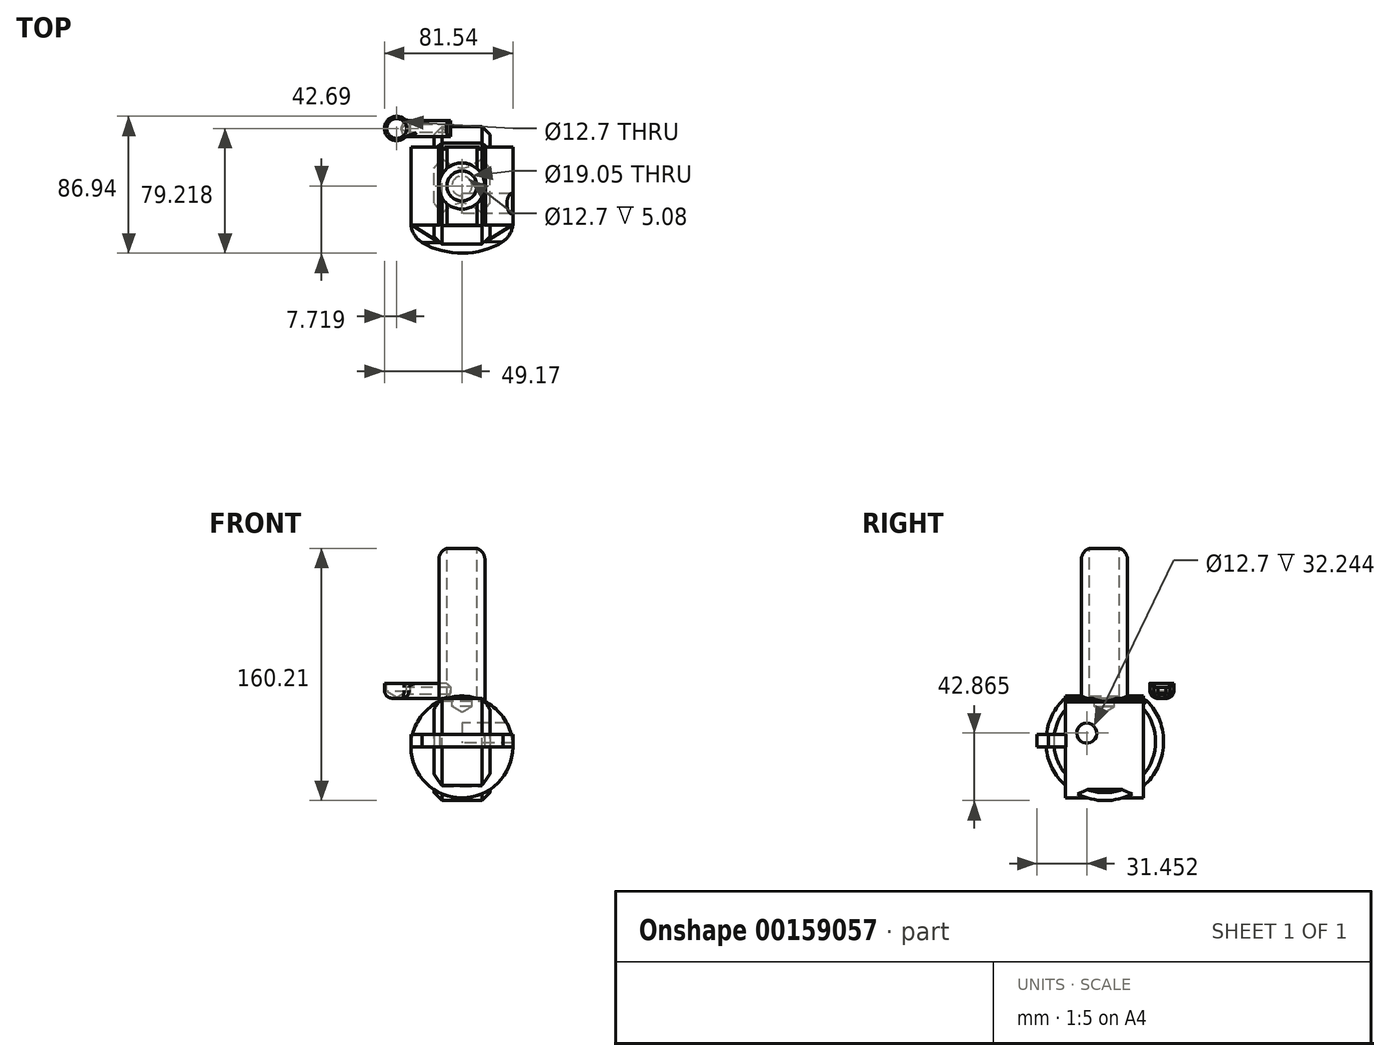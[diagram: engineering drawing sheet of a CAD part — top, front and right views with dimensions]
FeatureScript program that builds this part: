
annotation { "Feature Type Name" : "Feature", "Feature Type Description" : "" }
export const myFeature = defineFeature(function(context is Context, id is Id, definition is map)
    precondition{}
    {
        {
            var Q0;
            Q0=qCreatedBy(makeId("Top.planeOp"),FACE);
            var sketch = newSketch(context, id + "F0", { "sketchPlane" : qUnion([Q0])});
            skCircle(sketch, "E0", {"center": v(0, 0) * mm, "radius": 14.63 * mm});
            skSolve(sketch);
        }
        {
            var Q0;
            Q0=makeQuery(id+"F0.imprint","IMPRINT",FACE,{"disambiguationData":[TD([[makeQuery(id+"F0.imprint","IMPRINT",EDGE,{"derivedFrom":sQuery(id+"F0.wireOp",EDGE,"E0")}),1.0]])]});
            extrude(context, id + "F1", {"entities" : qUnion([Q0]), "depth" : 95.25 * mm});
        }
        {
            var Q0;
            Q0=qCreatedBy(makeId("Right.planeOp"),FACE);
            var sketch = newSketch(context, id + "F2", { "sketchPlane" : qUnion([Q0])});
            skArc(sketch, "E1", {"start": v(-25.08, 0) * mm, "mid": v(0.22, -64.96) * mm, "end": v(25.52, 0) * mm});
            skLineSegment(sketch, "E2", {"start": v(-25.08, 0) * mm, "end": v(25.52, 0) * mm});
            skSolve(sketch);
        }
        {
            var Q0;
            Q0 = qSketchRegion(id + "F2", true);
            extrude(context, id + "F3", {"entities" : qUnion([Q0]), "operationType" : NewBodyOperationType.ADD, "endBound" : BoundingType.SYMMETRIC, "oppositeDirection" : true, "depth" : 35.56 * mm});
        }
        {
            var Q0;
            Q0=makeQuery(id+"F1.opExtrude","CAP_FACE",FACE,{"disambiguationData":[OSD([sQuery(id+"F0.wireOp",EDGE,"E0")])],"isStart":false});
            var sketch = newSketch(context, id + "F4", { "sketchPlane" : qUnion([Q0])});
            skCircle(sketch, "E3", {"center": v(0, 0) * mm, "radius": 10 * mm});
            skSolve(sketch);
        }
        {
            var Q0;
            Q0=sQuery(id+"F4.wireOp",VERTEX,"E3.center");
            var Q1;
            Q1=makeQuery(id+"F1.opExtrude","SWEPT_BODY",BODY,{"disambiguationData":[OSD([sQuery(id+"F0.wireOp",EDGE,"E0")])]});
            hole(context, id + "F5", {"style" : HoleStyle.SIMPLE, "endStyle" : HoleEndStyle.BLIND, "holeDiameter" : 19.05 * mm, "holeDepth" : 139.7 * mm, "locations" : qUnion([Q0]), "scope" : qUnion([Q1])});
        }
        {
            var Q0;
            Q0=makeQuery(id+"F3.opExtrude","CAP_FACE",FACE,{"disambiguationData":[OSD([sQuery(id+"F2.wireOp",EDGE,"E1"),sQuery(id+"F2.wireOp",EDGE,"E2")])],"isStart":true});
            var sketch = newSketch(context, id + "F6", { "sketchPlane" : qUnion([Q0])});
            skCircle(sketch, "E4", {"center": v(18.07, -19.67) * mm, "radius": 8.9 * mm});
            skSolve(sketch);
        }
        {
            var Q0;
            Q0=sQuery(id+"F6.wireOp",VERTEX,"E4.center");
            var Q1;
            Q1=makeQuery(id+"F1.opExtrude","SWEPT_BODY",BODY,{"disambiguationData":[OSD([sQuery(id+"F0.wireOp",EDGE,"E0")])]});
            hole(context, id + "F7", {"style" : HoleStyle.SIMPLE, "endStyle" : HoleEndStyle.BLIND, "holeDiameter" : 12.7 * mm, "holeDepth" : 30.48 * mm, "locations" : qUnion([Q0]), "scope" : qUnion([Q1])});
        }
        {
            var Q0;
            Q0=qCreatedBy(makeId("Top.planeOp"),FACE);
            var sketch = newSketch(context, id + "F8", { "sketchPlane" : qUnion([Q0])});
            skLineSegment(sketch, "E5", {"start": v(-7.05, 41.62) * mm, "end": v(-35.65, 41.62) * mm});
            skLineSegment(sketch, "E6", {"start": v(-7.05, 41.62) * mm, "end": v(-7.05, 31.44) * mm});
            skLineSegment(sketch, "E7", {"start": v(-7.05, 31.44) * mm, "end": v(-35.65, 31.44) * mm});
            skArc(sketch, "E8", {"start": v(-35.65, 41.62) * mm, "mid": v(-49.17, 36.53) * mm, "end": v(-35.65, 31.44) * mm});
            skSolve(sketch);
        }
        {
            var Q0;
            Q0=makeQuery(id+"F8.imprint","IMPRINT",FACE,{"disambiguationData":[TD([[makeQuery(id+"F8.imprint","IMPRINT",EDGE,{"derivedFrom":sQuery(id+"F8.wireOp",EDGE,"E5")}),1.0]])]});
            extrude(context, id + "F9", {"entities" : qUnion([Q0]), "depth" : 9.52 * mm});
        }
        {
            var Q0;
            Q0=makeQuery(id+"F9.opExtrude","CAP_FACE",FACE,{"disambiguationData":[OSD([sQuery(id+"F8.wireOp",EDGE,"E5"),sQuery(id+"F8.wireOp",EDGE,"E6"),sQuery(id+"F8.wireOp",EDGE,"E7"),sQuery(id+"F8.wireOp",EDGE,"E8")])],"isStart":false});
            var sketch = newSketch(context, id + "F10", { "sketchPlane" : qUnion([Q0])});
            skCircle(sketch, "E9", {"center": v(-41.45, 36.53) * mm, "radius": 4.92 * mm});
            skSolve(sketch);
        }
        {
            var Q0;
            Q0=sQuery(id+"F10.wireOp",VERTEX,"E9.center");
            var Q1;
            Q1=makeQuery(id+"F9.opExtrude","SWEPT_BODY",BODY,{"disambiguationData":[OSD([sQuery(id+"F8.wireOp",EDGE,"E5"),sQuery(id+"F8.wireOp",EDGE,"E6"),sQuery(id+"F8.wireOp",EDGE,"E7"),sQuery(id+"F8.wireOp",EDGE,"E8")])]});
            hole(context, id + "F11", {"style" : HoleStyle.SIMPLE, "endStyle" : HoleEndStyle.BLIND, "holeDiameter" : 12.7 * mm, "holeDepth" : 5.08 * mm, "locations" : qUnion([Q0]), "scope" : qUnion([Q1])});
        }
        {
            var Q0;
            Q0=makeQuery(id+"F9.opExtrude","SWEPT_FACE",FACE,{"disambiguationData":[OSD([sQuery(id+"F8.wireOp",EDGE,"E6")])]});
            var Q1;
            Q1=makeQuery(id+"F11.hole-0.boolean.opBoolean","COPY",FACE,{"derivedFrom":makeQuery(id+"F11.hole-0.opRevolve","SWEPT_FACE",FACE,{"disambiguationData":[OSD([sQuery(id+"F11.hole-0.sketch.wireOp",EDGE,"core_line_2")])]})});
            shell(context, id + "F12", {"entities" : qUnion([Q0, Q1]), "thickness" : 2.54 * mm});
        }
        {
            var Q0;
            Q0=makeQuery(id+"F1.opExtrude","CAP_EDGE",EDGE,{"disambiguationData":[OSD([sQuery(id+"F0.wireOp",EDGE,"E0")])],"isStart":false});
            fillet(context, id + "F13", {"entities" : qUnion([Q0]), "radius" : 7.62 * mm, "tangentPropagation" : true, "allowEdgeOverflow" : false});
        }
        {
            var Q0;
            Q0=makeQuery(id+"F9.opExtrude","CAP_FACE",FACE,{"disambiguationData":[OSD([sQuery(id+"F8.wireOp",EDGE,"E5"),sQuery(id+"F8.wireOp",EDGE,"E6"),sQuery(id+"F8.wireOp",EDGE,"E7"),sQuery(id+"F8.wireOp",EDGE,"E8")])],"isStart":true});
            fillet(context, id + "F14", {"entities" : qUnion([Q0]), "radius" : 5.08 * mm, "tangentPropagation" : true, "allowEdgeOverflow" : false});
        }
        {
            var Q0;
            Q0=makeQuery(id+"F9.opExtrude","CAP_EDGE",EDGE,{"disambiguationData":[OSD([sQuery(id+"F8.wireOp",EDGE,"E6")])],"isStart":false});
            chamfer(context, id + "F15", {"entities" : qUnion([Q0]), "width" : 2.54 * mm, "tangentPropagation" : true});
        }
        {
            var Q0;
            Q0=makeQuery(id+"F9.opExtrude","CAP_EDGE",EDGE,{"disambiguationData":[OSD([sQuery(id+"F8.wireOp",EDGE,"E7")])],"isStart":false});
            var Q1;
            Q1=makeQuery(id+"F9.opExtrude","CAP_EDGE",EDGE,{"disambiguationData":[OSD([sQuery(id+"F8.wireOp",EDGE,"E5")])],"isStart":false});
            fillet(context, id + "F16", {"entities" : qUnion([Q0, Q1]), "radius" : 2.45 * mm, "tangentPropagation" : true, "allowEdgeOverflow" : false});
        }
        {
            var Q0;
            Q0=makeQuery(id+"F14.opFillet","BLEND_EDGE",EDGE,{"blendedFrom":[makeQuery(id+"F9.opExtrude","CAP_EDGE",EDGE,{"disambiguationData":[OSD([sQuery(id+"F8.wireOp",EDGE,"E5")])],"isStart":true}),makeQuery(id+"F9.opExtrude","CAP_EDGE",EDGE,{"disambiguationData":[OSD([sQuery(id+"F8.wireOp",EDGE,"E8")])],"isStart":true})],"blendedInto":[]});
            var Q1;
            Q1=makeQuery(id+"F16.opFillet","BLEND_EDGE",EDGE,{"blendedFrom":[makeQuery(id+"F9.opExtrude","CAP_EDGE",EDGE,{"disambiguationData":[OSD([sQuery(id+"F8.wireOp",EDGE,"E7")])],"isStart":false}),makeQuery(id+"F9.opExtrude","SWEPT_FACE",FACE,{"disambiguationData":[OSD([sQuery(id+"F8.wireOp",EDGE,"E8")])]})],"blendedInto":[makeQuery(id+"F9.opExtrude","SWEPT_FACE",FACE,{"disambiguationData":[OSD([sQuery(id+"F8.wireOp",EDGE,"E8")])]})]});
            var Q2;
            Q2=makeQuery(id+"F9.opExtrude","SWEPT_EDGE",EDGE,{"disambiguationData":[OSD([sQuery(id+"F8.wireOp",EDGE,"E7"),sQuery(id+"F8.wireOp",EDGE,"E8")])]});
            var Q3;
            Q3=makeQuery(id+"F14.opFillet","BLEND_EDGE",EDGE,{"blendedFrom":[makeQuery(id+"F9.opExtrude","CAP_EDGE",EDGE,{"disambiguationData":[OSD([sQuery(id+"F8.wireOp",EDGE,"E7")])],"isStart":true}),makeQuery(id+"F9.opExtrude","CAP_EDGE",EDGE,{"disambiguationData":[OSD([sQuery(id+"F8.wireOp",EDGE,"E8")])],"isStart":true})],"blendedInto":[]});
            var Q4;
            Q4=makeQuery(id+"F16.opFillet","BLEND_EDGE",EDGE,{"blendedFrom":[makeQuery(id+"F9.opExtrude","CAP_EDGE",EDGE,{"disambiguationData":[OSD([sQuery(id+"F8.wireOp",EDGE,"E5")])],"isStart":false}),makeQuery(id+"F9.opExtrude","SWEPT_FACE",FACE,{"disambiguationData":[OSD([sQuery(id+"F8.wireOp",EDGE,"E8")])]})],"blendedInto":[makeQuery(id+"F9.opExtrude","SWEPT_FACE",FACE,{"disambiguationData":[OSD([sQuery(id+"F8.wireOp",EDGE,"E8")])]})]});
            var Q5;
            Q5=makeQuery(id+"F9.opExtrude","SWEPT_EDGE",EDGE,{"disambiguationData":[OSD([sQuery(id+"F8.wireOp",EDGE,"E5"),sQuery(id+"F8.wireOp",EDGE,"E8")])]});
            fillet(context, id + "F17", {"entities" : qUnion([Q0, Q1, Q2, Q3, Q4, Q5]), "radius" : 5.08 * mm, "tangentPropagation" : true, "allowEdgeOverflow" : false});
        }
        {
            var Q0;
            Q0=makeQuery(id+"F3.opExtrude","CAP_EDGE",EDGE,{"disambiguationData":[OSD([sQuery(id+"F2.wireOp",EDGE,"E1")])],"isStart":true});
            var Q1;
            Q1=makeQuery(id+"F3.opExtrude","CAP_EDGE",EDGE,{"disambiguationData":[OSD([sQuery(id+"F2.wireOp",EDGE,"E2")])],"isStart":true});
            var Q2;
            {var subQ0=sQuery(id+"F2.wireOp",EDGE,"E2");var subQ1=sQuery(id+"F2.wireOp",EDGE,"E1");Q2=makeQuery(id+"F3.opExtrude","SWEPT_EDGE",EDGE,{"disambiguationData":[OSD([subQ1,subQ0]),TDD([makeQuery(id+"F2.imprint","INTERSECT",VERTEX,{"disambiguationData":[OD(1.0)],"derivedFrom":[subQ1,subQ0]})])]});}
            var Q3;
            Q3=makeQuery(id+"F3.opExtrude","CAP_EDGE",EDGE,{"disambiguationData":[OSD([sQuery(id+"F2.wireOp",EDGE,"E2")])],"isStart":false});
            var Q4;
            Q4=makeQuery(id+"F3.opExtrude","CAP_EDGE",EDGE,{"disambiguationData":[OSD([sQuery(id+"F2.wireOp",EDGE,"E1")])],"isStart":false});
            chamfer(context, id + "F18", {"entities" : qUnion([Q0, Q1, Q2, Q3, Q4]), "width" : 5.08 * mm, "tangentPropagation" : true});
        }
        {
            var Q0;
            Q0=qCreatedBy(makeId("Front.planeOp"),FACE);
            var sketch = newSketch(context, id + "F19", { "sketchPlane" : qUnion([Q0])});
            skCircle(sketch, "E10", {"center": v(0, -30.9) * mm, "radius": 32.34 * mm});
            skSolve(sketch);
        }
        {
            var Q0;
            Q0 = qSketchRegion(id + "F19", true);
            extrude(context, id + "F20", {"entities" : qUnion([Q0]), "operationType" : NewBodyOperationType.ADD, "endBound" : BoundingType.SYMMETRIC, "depth" : 49.53 * mm});
        }
        {
            var Q0;
            Q0=qCreatedBy(makeId("Right.planeOp"),FACE);
            var sketch = newSketch(context, id + "F21", { "sketchPlane" : qUnion([Q0])});
            skCircle(sketch, "E11", {"center": v(-11.24, -22.1) * mm, "radius": 6.4 * mm});
            skSolve(sketch);
        }
        {
            var Q0;
            Q0=sQuery(id+"F21.wireOp",VERTEX,"E11.center");
            var Q1;
            Q1=makeQuery(id+"F1.opExtrude","SWEPT_BODY",BODY,{"disambiguationData":[OSD([sQuery(id+"F0.wireOp",EDGE,"E0")])]});
            hole(context, id + "F22", {"style" : HoleStyle.SIMPLE, "endStyle" : HoleEndStyle.THROUGH, "oppositeDirection" : true, "holeDiameter" : 12.7 * mm, "locations" : qUnion([Q0]), "scope" : qUnion([Q1]), "isTappedThrough" : true});
        }
        {
            var Q0;
            Q0=qCreatedBy(makeId("Top.planeOp"),FACE);
            var sketch = newSketch(context, id + "F23", { "sketchPlane" : qUnion([Q0])});
            skCircle(sketch, "E12", {"center": v(0, 0) * mm, "radius": 7.96 * mm});
            skSolve(sketch);
        }
        {
            var Q0;
            Q0=sQuery(id+"F23.wireOp",VERTEX,"E12.center");
            var Q1;
            Q1=makeQuery(id+"F1.opExtrude","SWEPT_BODY",BODY,{"disambiguationData":[OSD([sQuery(id+"F0.wireOp",EDGE,"E0")])]});
            hole(context, id + "F24", {"style" : HoleStyle.SIMPLE, "endStyle" : HoleEndStyle.BLIND, "holeDiameter" : 12.7 * mm, "holeDepth" : 5.08 * mm, "locations" : qUnion([Q0]), "scope" : qUnion([Q1])});
        }
        {
            var Q0;
            {var subQ0=sQuery(id+"F2.wireOp",EDGE,"E2");var subQ1=sQuery(id+"F2.wireOp",EDGE,"E1");var subQ2=sQuery(id+"F19.wireOp",EDGE,"E10");var subQ3=makeQuery(id+"F2.imprint","INTERSECT",VERTEX,{"disambiguationData":[OD(1.0)],"derivedFrom":[subQ1,subQ0]});Q0=makeQuery(id+"F20.boolean.opBoolean","SPLIT",FACE,{"disambiguationData":[TD([makeQuery(id+"F3.opExtrude","SWEPT_FACE",FACE,{"disambiguationData":[OSD([subQ1])]}),makeQuery(id+"F3.opExtrude","CAP_FACE",FACE,{"disambiguationData":[OSD([subQ1,subQ0])],"isStart":true}),makeQuery(id+"F3.opExtrude","CAP_FACE",FACE,{"disambiguationData":[OSD([subQ1,subQ0])],"isStart":false}),makeQuery(id+"F18.opChamfer","BLEND_FACE",FACE,{"disambiguationData":[OSD([subQ1,subQ0]),TDD([makeQuery(id+"F3.opExtrude","CAP_VERTEX",VERTEX,{"disambiguationData":[OSD([subQ1,subQ0]),TDD([subQ3])],"isStart":true})])]}),makeQuery(id+"F18.opChamfer","BLEND_FACE",FACE,{"disambiguationData":[OSD([subQ1,subQ0]),TDD([makeQuery(id+"F3.opExtrude","CAP_VERTEX",VERTEX,{"disambiguationData":[OSD([subQ1,subQ0]),TDD([subQ3])],"isStart":false})])]}),makeQuery(id+"F18.opChamfer","BLEND_FACE",FACE,{"disambiguationData":[OSD([subQ1]),TDD([makeQuery(id+"F3.opExtrude","CAP_EDGE",EDGE,{"disambiguationData":[OSD([subQ1])],"isStart":true})])]}),makeQuery(id+"F18.opChamfer","BLEND_FACE",FACE,{"disambiguationData":[OSD([subQ1]),TDD([makeQuery(id+"F3.opExtrude","CAP_EDGE",EDGE,{"disambiguationData":[OSD([subQ1])],"isStart":false})])]}),makeQuery(id+"F18.opChamfer","BLEND_FACE",FACE,{"disambiguationData":[OSD([subQ0]),TDD([makeQuery(id+"F3.opExtrude","CAP_EDGE",EDGE,{"disambiguationData":[OSD([subQ0])],"isStart":true})])]}),makeQuery(id+"F18.opChamfer","BLEND_FACE",FACE,{"disambiguationData":[OSD([subQ0]),TDD([makeQuery(id+"F3.opExtrude","CAP_EDGE",EDGE,{"disambiguationData":[OSD([subQ0])],"isStart":false})])]}),makeQuery(id+"F20.opExtrude","CAP_FACE",FACE,{"disambiguationData":[OSD([subQ2])],"isStart":true}),makeQuery(id+"F20.opExtrude","CAP_FACE",FACE,{"disambiguationData":[OSD([subQ2])],"isStart":false})])],"derivedFrom":makeQuery(id+"F20.opExtrude","SWEPT_FACE",FACE,{"disambiguationData":[OSD([subQ2])]})});}
            var Q1;
            {var subQ0=sQuery(id+"F2.wireOp",EDGE,"E2");var subQ1=sQuery(id+"F2.wireOp",EDGE,"E1");Q1=makeQuery(id+"F20.boolean.opBoolean","SPLIT",FACE,{"disambiguationData":[TD([makeQuery(id+"F3.opExtrude","SWEPT_FACE",FACE,{"disambiguationData":[OSD([subQ0])]})])],"derivedFrom":makeQuery(id+"F3.opExtrude","SWEPT_FACE",FACE,{"disambiguationData":[OSD([subQ1])]})});}
            cPlane(context, id + "F25", {"entities" : qUnion([Q0, Q1]), "cplaneType" : CPlaneType.LINE_ANGLE, "offset" : 25.4 * mm, "angle" : 0 * degree, "width" : 152.4 * mm, "height" : 152.4 * mm});
        }
        {
            var Q0;
            Q0=qCreatedBy(id+"F25.planeOp",FACE);
            var sketch = newSketch(context, id + "F26", { "sketchPlane" : qUnion([Q0])});
            skArc(sketch, "E13", {"start": v(-12.62, 36.86) * mm, "mid": v(-25.54, 35.62) * mm, "end": v(-32.37, 24.58) * mm});
            skLineSegment(sketch, "E14", {"start": v(-32.37, 24.58) * mm, "end": v(-12.62, 36.86) * mm});
            skSolve(sketch);
        }
        {
            var Q0;
            Q0=makeQuery(id+"F26.imprint","IMPRINT",FACE,{"disambiguationData":[TD([[makeQuery(id+"F26.imprint","IMPRINT",EDGE,{"derivedFrom":sQuery(id+"F26.wireOp",EDGE,"E13")}),1.0]])]});
            var Q1;
            Q1=sQuery(id+"F26.wireOp",EDGE,"E13");
            extrude(context, id + "F27", {"entities" : qUnion([Q0]), "surfaceEntities" : qUnion([Q1]), "oppositeDirection" : true, "depth" : 7.94 * mm});
        }
        {
            var Q0;
            Q0=makeQuery(id+"F27.opExtrude","SWEPT_BODY",BODY,{"disambiguationData":[OSD([sQuery(id+"F26.wireOp",EDGE,"E13"),sQuery(id+"F26.wireOp",EDGE,"E14")])]});
            var Q1;
            Q1=qCreatedBy(makeId("Right.planeOp"),FACE);
            mirror(context, id + "F28", {"operationType" : NewBodyOperationType.ADD, "entities" : qUnion([Q0]), "mirrorPlane" : qUnion([Q1])});
        }
        {
            var Q0;
            Q0=qCreatedBy(id+"F25.planeOp",FACE);
            var sketch = newSketch(context, id + "F29", { "sketchPlane" : qUnion([Q0])});
            skArc(sketch, "E15", {"start": v(26.16, 35.43) * mm, "mid": v(0.5, 42.69) * mm, "end": v(-25.3, 36) * mm});
            skLineSegment(sketch, "E16", {"start": v(26.16, 35.43) * mm, "end": v(-25.3, 36) * mm});
            skSolve(sketch);
        }
        {
            var Q0;
            Q0 = qSketchRegion(id + "F29", true);
            extrude(context, id + "F30", {"entities" : qUnion([Q0]), "operationType" : NewBodyOperationType.ADD, "oppositeDirection" : true, "depth" : 8.06 * mm});
        }
    });
